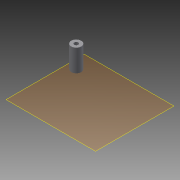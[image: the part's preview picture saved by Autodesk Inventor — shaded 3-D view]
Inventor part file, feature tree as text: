
AUTODESK INVENTOR PART (.ipt)
format: ipt  version: 2015 (Build 190159000, 159)  size: 78,848 bytes
history: native  units: mm
features: plane x2, extrude x1
ambient origin geometry x8: Origin, YZ Plane, XZ Plane, XY Plane, X Axis, Y Axis, Z Axis, Center Point
bodies: Solid1 (feature_tree)
feature tree (3):
  plane  "Work Plane1"
  plane  "Work Plane2"
  extrude  "Extrusion1"  Depth=10.0mm
